# Revit family: KDW010073
name_source: partatom
category: Plumbing Fixtures
revit_build: Autodesk Revit 2015 (Build: 20140606_1530(x64)
units: mm (PartAtom-declared; Revit-internal decimal feet)

## types (1)
- SILENIO AUFSATZWASCHTISCH 3042 460x600
    Accessory = Yes
    BIMobject category = Basins
    Brand url = http://www.kaldewei.com
    Color = https://www.kaldewei.co.uk
    ColourOptions = https://www.kaldewei.co.uk
    Design country = Germany
    Durability = https://www.kaldewei.de
    Edition number = 1
    Features = https://www.kaldewei.co.uk
    Finish = https://n
    Finition = Kaldewei
    HasGrabHandles = https://www.kaldewei.co.uk
    IFC Classification = Furnishing Element
    IfcExportAs = WASHHANDBASIN
    IfcExportType = IfcSanitaryTerminalType
    IntegralAccessories = https://www.kaldewei.co.uk
    Manufacturer = Kaldewei
    Manufacturer country = Germany
    ManufacturerCountry = GERMANY
    ManufacturerName = KALDEWEI
    ManufacturerURL = https://www.kaldewei.com
    Material = steel enamel
    Material main = Steel
    Material secondary = Enamel
    Metal = Chrome
    Model = SILENIOAUFSATZWASCHTISCH
    NBS Reference Code = 35-65-70-94
    NBS Reference Description = Wash Basin Systems
    Name = SILENIO
    Nominal height = 600 cm
    Nominal width = 460 cm
    NominalLength = 600
    ObjectName = SILENIO 460x600
    ObjectNorm = EN 14688EU DECLARATION OF PERFORMANCE(https://www.kaldewei.de
    ObjectPicture = https://www.kaldewei.co.uk
    ObjectURL = https://www.kaldewei.co.uk
    Polantis code = KDW010073
    Product Guid = a299122c-70f7-4958-a024-263185a41371
    Product SKU = 3042
    Product certification = https://www.kaldewei.co.uk
    Product data url = https://bimobject.com
    Product family = SILENIO
    Product group = Washbasin
    Product url = https://www.kaldewei.co.uk
    ProductInformation = Model No.3042: - fluid and sensually modern design all at once- optimum comfort through generous dimensioning of the washbasin- soft, organic interior shape- geometry allows fittings with short spout leaving ample space for washing- together with the SILENIO bath and SCONA shower surface, they form a perfect bathroom fitted out entirely with steel enamel- SILENIO washbasins are available now with or without overflow.- All SILENIO washbasins of 120 cm width are available now with 1x1 or 1x3 tap holes.- designed by Anke Salomon
    QR code = http://bimobject.com
    Revision = 1
    SerialNumber = 3042
    Shape = Inset Countertop
    Size = 460x600
    SupportFrame = https://www.kaldewei.co.uk
    Sustainability = https://kaldewei-fa.secure.footprint.net
    Technical description = https://www.kaldewei.co.uk
    TechnicalDataURL = https://kaldewei.typo-live.web-factory.de
    Type Comments = SILENIO AUFSATZWASCHTISCH 3042 460x600
    UNSPSC Code = 301815
    UNSPSCCode = 30181504
    UNSPSCNames = Sinks
    URL = https://www.kaldewei.co.uk
    Uniclass 1.4 Code = L7212
    Uniclass 1.4 Description = Washbasins
    Uniclass 2.0 Code = SS-35-65-70-94
    Uniclass 2.0 Description = Wash Basin Systems
    Uniclass 2015 = Pr_40_20_96
    Version = 4
    WarrantyDurationParts = 30
    WarrantyDurationUnit = Year
    WarrantyStartDate = https://www.kaldewei.co.uk
    Weight = 12,7
    Weight Net (Kg) = 12.7

## geometry (parser evidence)
native form markers: Sweep x3
no freeform markers — native parametric forms only
